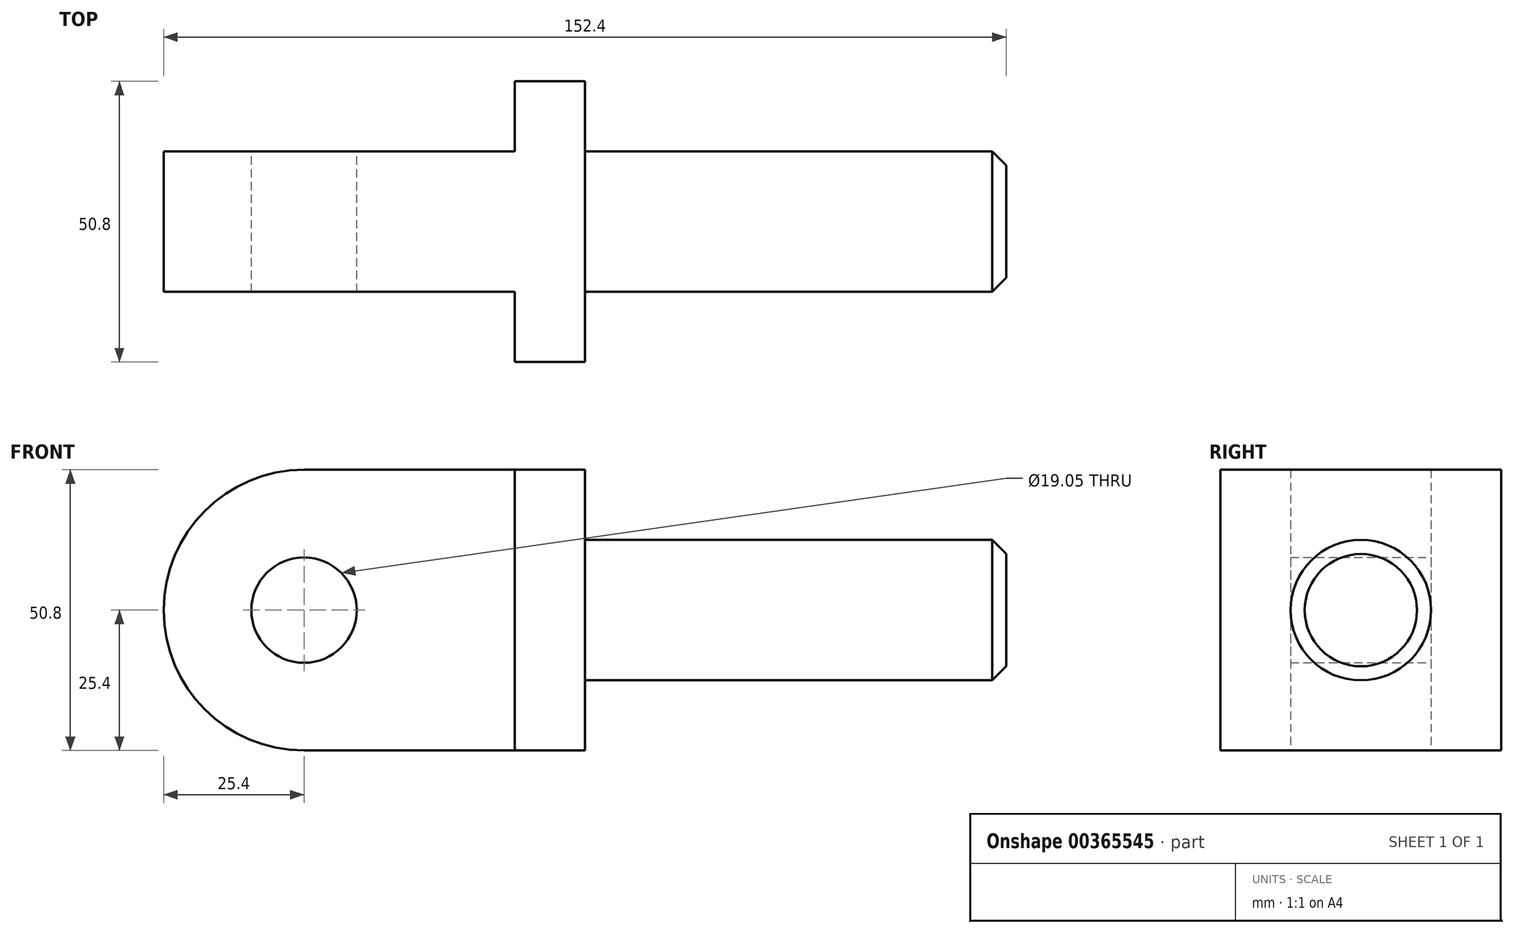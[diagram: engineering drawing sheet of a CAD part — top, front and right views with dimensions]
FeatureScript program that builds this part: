
annotation { "Feature Type Name" : "Feature", "Feature Type Description" : "" }
export const myFeature = defineFeature(function(context is Context, id is Id, definition is map)
    precondition{}
    {
        {
            var Q0;
            Q0=qCreatedBy(makeId("Front.planeOp"),FACE);
            var sketch = newSketch(context, id + "F0", { "sketchPlane" : qUnion([Q0])});
            skArc(sketch, "E0", {"start": v(0, 25.4) * mm, "mid": v(-25.4, 0) * mm, "end": v(0, -25.4) * mm});
            skCircle(sketch, "E1", {"center": v(0, 0) * mm, "radius": 9.53 * mm});
            skLineSegment(sketch, "E2", {"start": v(0, 25.4) * mm, "end": v(50.8, 25.4) * mm});
            skLineSegment(sketch, "E3", {"start": v(50.8, 25.4) * mm, "end": v(50.8, -25.4) * mm});
            skLineSegment(sketch, "E4", {"start": v(50.8, -25.4) * mm, "end": v(0, -25.4) * mm});
            skSolve(sketch);
        }
        {
            var Q0;
            Q0 = qSketchRegion(id + "F0", true);
            extrude(context, id + "F1", {"entities" : qUnion([Q0]), "endBound" : BoundingType.SYMMETRIC, "depth" : 50.8 * mm});
        }
        {
            var Q0;
            Q0=qCreatedBy(makeId("Right.planeOp"),FACE);
            var sketch = newSketch(context, id + "F2", { "sketchPlane" : qUnion([Q0])});
            skLineSegment(sketch, "E5.bottom", {"start": v(25.4, 25.4) * mm, "end": v(12.7, 25.4) * mm});
            skLineSegment(sketch, "E5.top", {"start": v(25.4, -25.4) * mm, "end": v(12.7, -25.4) * mm});
            skLineSegment(sketch, "E5.left", {"start": v(25.4, 25.4) * mm, "end": v(25.4, -25.4) * mm});
            skLineSegment(sketch, "E5.right", {"start": v(12.7, 25.4) * mm, "end": v(12.7, -25.4) * mm});
            skLineSegment(sketch, "E6.bottom", {"start": v(-12.7, 25.4) * mm, "end": v(-25.4, 25.4) * mm});
            skLineSegment(sketch, "E6.top", {"start": v(-12.7, -25.4) * mm, "end": v(-25.4, -25.4) * mm});
            skLineSegment(sketch, "E6.left", {"start": v(-12.7, 25.4) * mm, "end": v(-12.7, -25.4) * mm});
            skLineSegment(sketch, "E6.right", {"start": v(-25.4, 25.4) * mm, "end": v(-25.4, -25.4) * mm});
            skSolve(sketch);
        }
        {
            var Q0;
            Q0 = qSketchRegion(id + "F2", true);
            extrude(context, id + "F3", {"entities" : qUnion([Q0]), "operationType" : NewBodyOperationType.REMOVE, "depth" : 38.1 * mm});
        }
        {
            var Q0;
            Q0=makeQuery(id+"F2.imprint","IMPRINT",FACE,{"disambiguationData":[TD([[makeQuery(id+"F2.imprint","IMPRINT",EDGE,{"derivedFrom":sQuery(id+"F2.wireOp",EDGE,"E5.bottom")}),1.0]])]});
            var Q1;
            Q1=makeQuery(id+"F2.imprint","IMPRINT",FACE,{"disambiguationData":[TD([[makeQuery(id+"F2.imprint","IMPRINT",EDGE,{"derivedFrom":sQuery(id+"F2.wireOp",EDGE,"E6.bottom")}),1.0]])]});
            extrude(context, id + "F4", {"entities" : qUnion([Q0, Q1]), "operationType" : NewBodyOperationType.REMOVE, "oppositeDirection" : true, "depth" : 25.4 * mm});
        }
        {
            var Q0;
            Q0=makeQuery(id+"F1.opExtrude","SWEPT_FACE",FACE,{"disambiguationData":[OSD([sQuery(id+"F0.wireOp",EDGE,"E3")])]});
            var sketch = newSketch(context, id + "F5", { "sketchPlane" : qUnion([Q0])});
            skCircle(sketch, "E7", {"center": v(0, 0) * mm, "radius": 12.7 * mm});
            skSolve(sketch);
        }
        {
            var Q0;
            Q0 = qSketchRegion(id + "F5", true);
            extrude(context, id + "F6", {"entities" : qUnion([Q0]), "operationType" : NewBodyOperationType.ADD, "depth" : 76.2 * mm});
        }
        {
            var Q0;
            Q0=makeQuery(id+"F6.opExtrude","CAP_EDGE",EDGE,{"disambiguationData":[OSD([sQuery(id+"F5.wireOp",EDGE,"E7")])],"isStart":false});
            chamfer(context, id + "F7", {"entities" : qUnion([Q0]), "chamferType" : ChamferType.OFFSET_ANGLE, "width" : 2.54 * mm, "oppositeDirection" : false, "angle" : 45 * degree, "tangentPropagation" : true});
        }
    });
